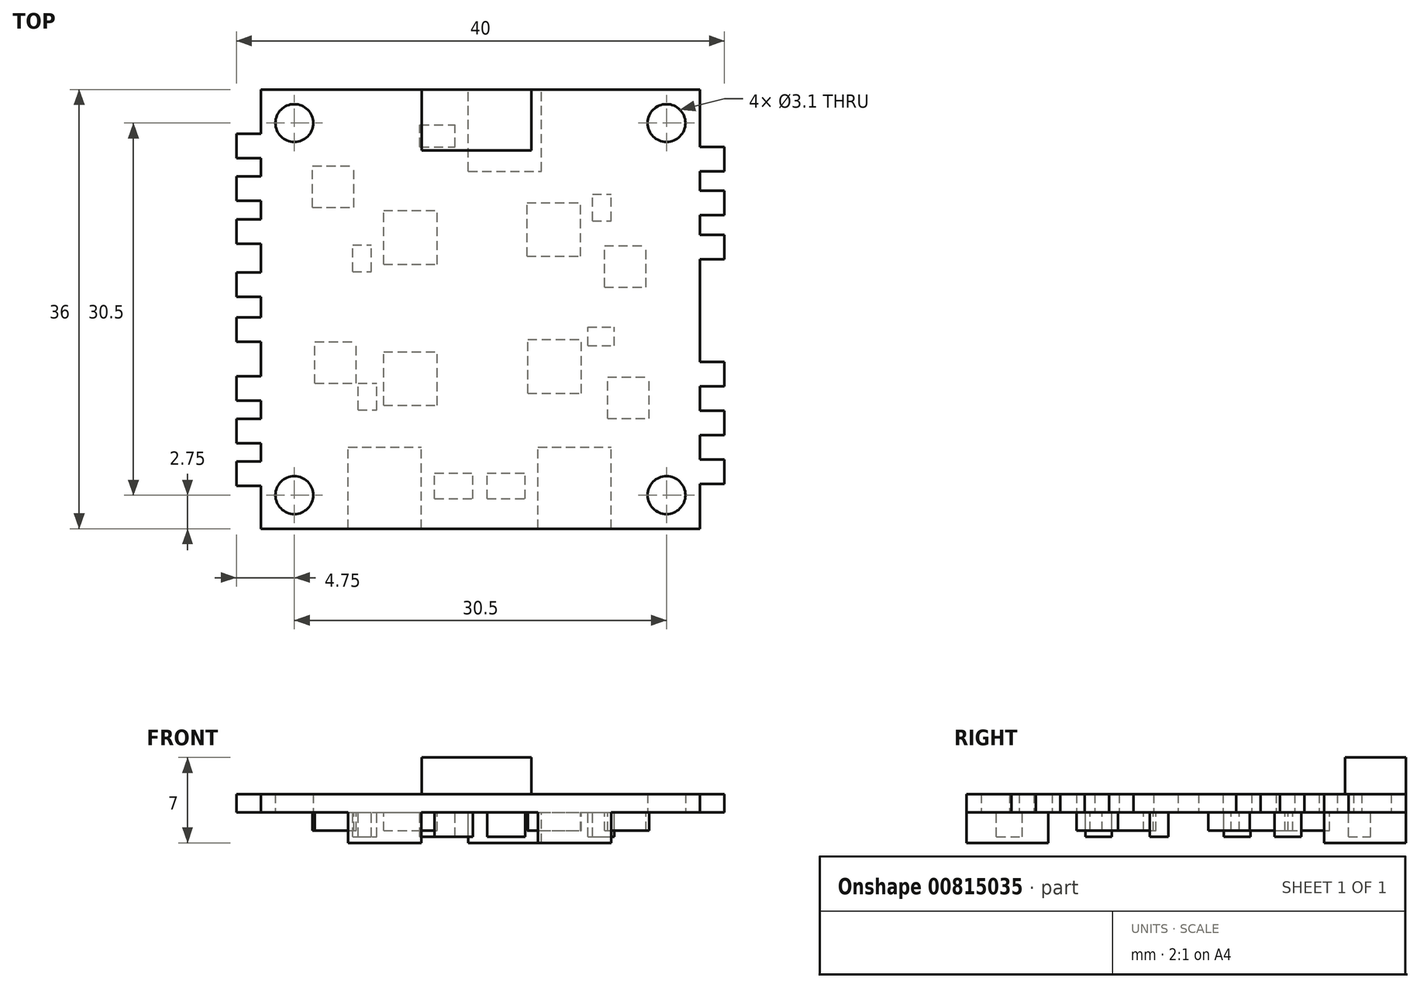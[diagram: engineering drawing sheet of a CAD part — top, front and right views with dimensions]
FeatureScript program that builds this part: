
annotation { "Feature Type Name" : "Feature", "Feature Type Description" : "" }
export const myFeature = defineFeature(function(context is Context, id is Id, definition is map)
    precondition{}
    {
        {
            var Q0;
            Q0=qCreatedBy(makeId("Top.planeOp"),FACE);
            var sketch = newSketch(context, id + "F0", { "sketchPlane" : qUnion([Q0])});
            skLineSegment(sketch, "E0", {"start": v(-20.18, -18) * mm, "end": v(20.18, 18) * mm, "construction": true});
            skPoint(sketch, "E1", {"position": v(-15.42, 15.08) * mm});
            skPoint(sketch, "E2", {"position": v(-15.47, -15.18) * mm});
            skPoint(sketch, "E3", {"position": v(14.98, 15.03) * mm});
            skPoint(sketch, "E4", {"position": v(15.18, -15.28) * mm});
            skSolve(sketch);
        }
        {
            var Q0;
            Q0=qCreatedBy(makeId("Top.planeOp"),FACE);
            var sketch = newSketch(context, id + "F1", { "sketchPlane" : qUnion([Q0])});
            skLineSegment(sketch, "E5", {"start": v(-20.13, -18) * mm, "end": v(20.13, 18) * mm, "construction": true});
            skSolve(sketch);
        }
        {
            var Q0;
            Q0=qCreatedBy(makeId("Top.planeOp"),FACE);
            var sketch = newSketch(context, id + "F2", { "sketchPlane" : qUnion([Q0])});
            skLineSegment(sketch, "E6.bottom", {"start": v(-18, 18) * mm, "end": v(18, 18) * mm});
            skLineSegment(sketch, "E6.top", {"start": v(-18, -18) * mm, "end": v(18, -18) * mm});
            skLineSegment(sketch, "E6.left", {"start": v(-18, 18) * mm, "end": v(-18, -18) * mm});
            skLineSegment(sketch, "E6.right", {"start": v(18, 18) * mm, "end": v(18, -18) * mm});
            skLineSegment(sketch, "E7", {"start": v(-18, 18) * mm, "end": v(18, -18) * mm, "construction": true});
            skLineSegment(sketch, "E8.bottom", {"start": v(-20, 14.37) * mm, "end": v(-18, 14.37) * mm});
            skLineSegment(sketch, "E8.top", {"start": v(-20, 12.37) * mm, "end": v(-18, 12.37) * mm});
            skLineSegment(sketch, "E8.left", {"start": v(-20, 14.37) * mm, "end": v(-20, 12.37) * mm});
            skLineSegment(sketch, "E8.right", {"start": v(-18, 14.37) * mm, "end": v(-18, 12.37) * mm});
            skLineSegment(sketch, "E9.1.0.0", {"start": v(-20, 10.87) * mm, "end": v(-18, 10.87) * mm});
            skLineSegment(sketch, "E9.1.0.1", {"start": v(-20, 8.87) * mm, "end": v(-18, 8.87) * mm});
            skLineSegment(sketch, "E9.1.0.2", {"start": v(-20, 10.87) * mm, "end": v(-20, 8.87) * mm});
            skLineSegment(sketch, "E9.1.0.3", {"start": v(-18, 10.87) * mm, "end": v(-18, 8.87) * mm});
            skLineSegment(sketch, "E9.2.0.0", {"start": v(-20, 7.37) * mm, "end": v(-18, 7.37) * mm});
            skLineSegment(sketch, "E9.2.0.1", {"start": v(-20, 5.37) * mm, "end": v(-18, 5.37) * mm});
            skLineSegment(sketch, "E9.2.0.2", {"start": v(-20, 7.37) * mm, "end": v(-20, 5.37) * mm});
            skLineSegment(sketch, "E9.2.0.3", {"start": v(-18, 7.37) * mm, "end": v(-18, 5.37) * mm});
            skLineSegment(sketch, "E9.direction1", {"start": v(-20, 12.37) * mm, "end": v(-20, 8.87) * mm, "construction": true});
            skLineSegment(sketch, "E10.bottom", {"start": v(-20, -5.5) * mm, "end": v(-18, -5.5) * mm});
            skLineSegment(sketch, "E10.top", {"start": v(-20, -7.5) * mm, "end": v(-18, -7.5) * mm});
            skLineSegment(sketch, "E10.left", {"start": v(-20, -5.5) * mm, "end": v(-20, -7.5) * mm});
            skLineSegment(sketch, "E10.right", {"start": v(-18, -5.5) * mm, "end": v(-18, -7.5) * mm});
            skLineSegment(sketch, "E11.1.0.0", {"start": v(-20, -9) * mm, "end": v(-18, -9) * mm});
            skLineSegment(sketch, "E11.1.0.1", {"start": v(-20, -11) * mm, "end": v(-18, -11) * mm});
            skLineSegment(sketch, "E11.1.0.2", {"start": v(-20, -9) * mm, "end": v(-20, -11) * mm});
            skLineSegment(sketch, "E11.1.0.3", {"start": v(-18, -9) * mm, "end": v(-18, -11) * mm});
            skLineSegment(sketch, "E11.2.0.0", {"start": v(-20, -12.5) * mm, "end": v(-18, -12.5) * mm});
            skLineSegment(sketch, "E11.2.0.1", {"start": v(-20, -14.5) * mm, "end": v(-18, -14.5) * mm});
            skLineSegment(sketch, "E11.2.0.2", {"start": v(-20, -12.5) * mm, "end": v(-20, -14.5) * mm});
            skLineSegment(sketch, "E11.2.0.3", {"start": v(-18, -12.5) * mm, "end": v(-18, -14.5) * mm});
            skLineSegment(sketch, "E11.direction1", {"start": v(-20, -7.5) * mm, "end": v(-20, -11) * mm, "construction": true});
            skLineSegment(sketch, "E12.bottom", {"start": v(18, 13.3) * mm, "end": v(20, 13.3) * mm});
            skLineSegment(sketch, "E12.top", {"start": v(18, 11.3) * mm, "end": v(20, 11.3) * mm});
            skLineSegment(sketch, "E12.left", {"start": v(18, 13.3) * mm, "end": v(18, 11.3) * mm});
            skLineSegment(sketch, "E12.right", {"start": v(20, 13.3) * mm, "end": v(20, 11.3) * mm});
            skLineSegment(sketch, "E13.1.0.0", {"start": v(18, 9.7) * mm, "end": v(20, 9.7) * mm});
            skLineSegment(sketch, "E13.1.0.1", {"start": v(18, 7.7) * mm, "end": v(20, 7.7) * mm});
            skLineSegment(sketch, "E13.1.0.2", {"start": v(18, 9.7) * mm, "end": v(18, 7.7) * mm});
            skLineSegment(sketch, "E13.1.0.3", {"start": v(20, 9.7) * mm, "end": v(20, 7.7) * mm});
            skLineSegment(sketch, "E13.2.0.0", {"start": v(18, 6.1) * mm, "end": v(20, 6.1) * mm});
            skLineSegment(sketch, "E13.2.0.1", {"start": v(18, 4.1) * mm, "end": v(20, 4.1) * mm});
            skLineSegment(sketch, "E13.2.0.2", {"start": v(18, 6.1) * mm, "end": v(18, 4.1) * mm});
            skLineSegment(sketch, "E13.2.0.3", {"start": v(20, 6.1) * mm, "end": v(20, 4.1) * mm});
            skLineSegment(sketch, "E13.direction1", {"start": v(18, 11.3) * mm, "end": v(18, 7.7) * mm, "construction": true});
            skLineSegment(sketch, "E14.bottom", {"start": v(18, -4.32) * mm, "end": v(20, -4.32) * mm});
            skLineSegment(sketch, "E14.top", {"start": v(18, -6.32) * mm, "end": v(20, -6.32) * mm});
            skLineSegment(sketch, "E14.left", {"start": v(18, -4.32) * mm, "end": v(18, -6.32) * mm});
            skLineSegment(sketch, "E14.right", {"start": v(20, -4.32) * mm, "end": v(20, -6.32) * mm});
            skLineSegment(sketch, "E15.1.0.0", {"start": v(18, -8.32) * mm, "end": v(20, -8.32) * mm});
            skLineSegment(sketch, "E15.1.0.1", {"start": v(18, -10.32) * mm, "end": v(20, -10.32) * mm});
            skLineSegment(sketch, "E15.1.0.2", {"start": v(18, -8.32) * mm, "end": v(18, -10.32) * mm});
            skLineSegment(sketch, "E15.1.0.3", {"start": v(20, -8.32) * mm, "end": v(20, -10.32) * mm});
            skLineSegment(sketch, "E15.2.0.0", {"start": v(18, -12.32) * mm, "end": v(20, -12.32) * mm});
            skLineSegment(sketch, "E15.2.0.1", {"start": v(18, -14.32) * mm, "end": v(20, -14.32) * mm});
            skLineSegment(sketch, "E15.2.0.2", {"start": v(18, -12.32) * mm, "end": v(18, -14.32) * mm});
            skLineSegment(sketch, "E15.2.0.3", {"start": v(20, -12.32) * mm, "end": v(20, -14.32) * mm});
            skLineSegment(sketch, "E15.direction1", {"start": v(18, -6.32) * mm, "end": v(18, -10.32) * mm, "construction": true});
            skLineSegment(sketch, "E16.bottom", {"start": v(15.25, -15.25) * mm, "end": v(-15.25, -15.25) * mm, "construction": true});
            skLineSegment(sketch, "E16.top", {"start": v(15.25, 15.25) * mm, "end": v(-15.25, 15.25) * mm, "construction": true});
            skLineSegment(sketch, "E16.left", {"start": v(15.25, -15.25) * mm, "end": v(15.25, 15.25) * mm, "construction": true});
            skLineSegment(sketch, "E16.right", {"start": v(-15.25, -15.25) * mm, "end": v(-15.25, 15.25) * mm, "construction": true});
            skPoint(sketch, "E16.middle", {"position": v(0, 0) * mm});
            skCircle(sketch, "E17", {"center": v(-15.25, 15.25) * mm, "radius": 1.55 * mm});
            skCircle(sketch, "E18", {"center": v(15.25, 15.25) * mm, "radius": 1.55 * mm});
            skCircle(sketch, "E19", {"center": v(15.25, -15.25) * mm, "radius": 1.55 * mm});
            skCircle(sketch, "E20", {"center": v(-15.25, -15.25) * mm, "radius": 1.55 * mm});
            skLineSegment(sketch, "E21.2.0.0", {"start": v(-20, -0.67) * mm, "end": v(-18, -0.67) * mm});
            skLineSegment(sketch, "E21.2.0.1", {"start": v(-20, -2.67) * mm, "end": v(-18, -2.67) * mm});
            skLineSegment(sketch, "E21.2.0.2", {"start": v(-20, -0.67) * mm, "end": v(-20, -2.67) * mm});
            skLineSegment(sketch, "E21.2.0.3", {"start": v(-18, -0.67) * mm, "end": v(-18, -2.67) * mm});
            skLineSegment(sketch, "E22.2.0.0", {"start": v(-20, 3) * mm, "end": v(-18, 3) * mm});
            skLineSegment(sketch, "E22.2.0.1", {"start": v(-20, 1) * mm, "end": v(-18, 1) * mm});
            skLineSegment(sketch, "E22.2.0.2", {"start": v(-20, 3) * mm, "end": v(-20, 1) * mm});
            skLineSegment(sketch, "E22.2.0.3", {"start": v(-18, 3) * mm, "end": v(-18, 1) * mm});
            skSolve(sketch);
        }
        {
            var Q0;
            Q0 = qSketchRegion(id + "F2", true);
            extrude(context, id + "F3", {"entities" : qUnion([Q0]), "depth" : 1.5 * mm, "offsetDistance" : 25 * mm});
        }
        {
            var Q0;
            Q0=makeQuery(id+"F3.opExtrude","CAP_FACE",FACE,{"disambiguationData":[OSD([sQuery(id+"F2.wireOp",EDGE,"E6.bottom"),sQuery(id+"F2.wireOp",EDGE,"E6.top"),sQuery(id+"F2.wireOp",EDGE,"E6.left"),sQuery(id+"F2.wireOp",EDGE,"E6.right"),sQuery(id+"F2.wireOp",EDGE,"E8.bottom"),sQuery(id+"F2.wireOp",EDGE,"E8.top"),sQuery(id+"F2.wireOp",EDGE,"E8.left"),sQuery(id+"F2.wireOp",EDGE,"E9.1.0.0"),sQuery(id+"F2.wireOp",EDGE,"E9.1.0.1"),sQuery(id+"F2.wireOp",EDGE,"E9.1.0.2"),sQuery(id+"F2.wireOp",EDGE,"E9.2.0.0"),sQuery(id+"F2.wireOp",EDGE,"E9.2.0.1"),sQuery(id+"F2.wireOp",EDGE,"E9.2.0.2"),sQuery(id+"F2.wireOp",EDGE,"E10.bottom"),sQuery(id+"F2.wireOp",EDGE,"E10.top"),sQuery(id+"F2.wireOp",EDGE,"E10.left"),sQuery(id+"F2.wireOp",EDGE,"E11.1.0.0"),sQuery(id+"F2.wireOp",EDGE,"E11.1.0.1"),sQuery(id+"F2.wireOp",EDGE,"E11.1.0.2"),sQuery(id+"F2.wireOp",EDGE,"E11.2.0.0"),sQuery(id+"F2.wireOp",EDGE,"E11.2.0.1"),sQuery(id+"F2.wireOp",EDGE,"E11.2.0.2"),sQuery(id+"F2.wireOp",EDGE,"E12.bottom"),sQuery(id+"F2.wireOp",EDGE,"E12.top"),sQuery(id+"F2.wireOp",EDGE,"E12.right"),sQuery(id+"F2.wireOp",EDGE,"E13.1.0.0"),sQuery(id+"F2.wireOp",EDGE,"E13.1.0.1"),sQuery(id+"F2.wireOp",EDGE,"E13.1.0.3"),sQuery(id+"F2.wireOp",EDGE,"E13.2.0.0"),sQuery(id+"F2.wireOp",EDGE,"E13.2.0.1"),sQuery(id+"F2.wireOp",EDGE,"E13.2.0.3"),sQuery(id+"F2.wireOp",EDGE,"E14.bottom"),sQuery(id+"F2.wireOp",EDGE,"E14.top"),sQuery(id+"F2.wireOp",EDGE,"E14.right"),sQuery(id+"F2.wireOp",EDGE,"E15.1.0.0"),sQuery(id+"F2.wireOp",EDGE,"E15.1.0.1"),sQuery(id+"F2.wireOp",EDGE,"E15.1.0.3"),sQuery(id+"F2.wireOp",EDGE,"E15.2.0.0"),sQuery(id+"F2.wireOp",EDGE,"E15.2.0.1"),sQuery(id+"F2.wireOp",EDGE,"E15.2.0.3"),sQuery(id+"F2.wireOp",EDGE,"E17"),sQuery(id+"F2.wireOp",EDGE,"E18"),sQuery(id+"F2.wireOp",EDGE,"E19"),sQuery(id+"F2.wireOp",EDGE,"E20")])],"isStart":false});
            var sketch = newSketch(context, id + "F4", { "sketchPlane" : qUnion([Q0])});
            skLineSegment(sketch, "E23.bottom", {"start": v(-4.82, 18) * mm, "end": v(4.18, 18) * mm});
            skLineSegment(sketch, "E23.top", {"start": v(-4.82, 13) * mm, "end": v(4.18, 13) * mm});
            skLineSegment(sketch, "E23.left", {"start": v(-4.82, 18) * mm, "end": v(-4.82, 13) * mm});
            skLineSegment(sketch, "E23.right", {"start": v(4.18, 18) * mm, "end": v(4.18, 13) * mm});
            skSolve(sketch);
        }
        {
            var Q0;
            Q0 = qSketchRegion(id + "F4", true);
            extrude(context, id + "F5", {"entities" : qUnion([Q0]), "operationType" : NewBodyOperationType.ADD, "depth" : 3 * mm, "offsetDistance" : 25 * mm});
        }
        {
            var Q0;
            Q0=makeQuery(id+"F3.opExtrude","CAP_FACE",FACE,{"disambiguationData":[OSD([sQuery(id+"F2.wireOp",EDGE,"E6.bottom"),sQuery(id+"F2.wireOp",EDGE,"E6.top"),sQuery(id+"F2.wireOp",EDGE,"E6.left"),sQuery(id+"F2.wireOp",EDGE,"E6.right"),sQuery(id+"F2.wireOp",EDGE,"E8.bottom"),sQuery(id+"F2.wireOp",EDGE,"E8.top"),sQuery(id+"F2.wireOp",EDGE,"E8.left"),sQuery(id+"F2.wireOp",EDGE,"E9.1.0.0"),sQuery(id+"F2.wireOp",EDGE,"E9.1.0.1"),sQuery(id+"F2.wireOp",EDGE,"E9.1.0.2"),sQuery(id+"F2.wireOp",EDGE,"E9.2.0.0"),sQuery(id+"F2.wireOp",EDGE,"E9.2.0.1"),sQuery(id+"F2.wireOp",EDGE,"E9.2.0.2"),sQuery(id+"F2.wireOp",EDGE,"E10.bottom"),sQuery(id+"F2.wireOp",EDGE,"E10.top"),sQuery(id+"F2.wireOp",EDGE,"E10.left"),sQuery(id+"F2.wireOp",EDGE,"E11.1.0.0"),sQuery(id+"F2.wireOp",EDGE,"E11.1.0.1"),sQuery(id+"F2.wireOp",EDGE,"E11.1.0.2"),sQuery(id+"F2.wireOp",EDGE,"E11.2.0.0"),sQuery(id+"F2.wireOp",EDGE,"E11.2.0.1"),sQuery(id+"F2.wireOp",EDGE,"E11.2.0.2"),sQuery(id+"F2.wireOp",EDGE,"E12.bottom"),sQuery(id+"F2.wireOp",EDGE,"E12.top"),sQuery(id+"F2.wireOp",EDGE,"E12.right"),sQuery(id+"F2.wireOp",EDGE,"E13.1.0.0"),sQuery(id+"F2.wireOp",EDGE,"E13.1.0.1"),sQuery(id+"F2.wireOp",EDGE,"E13.1.0.3"),sQuery(id+"F2.wireOp",EDGE,"E13.2.0.0"),sQuery(id+"F2.wireOp",EDGE,"E13.2.0.1"),sQuery(id+"F2.wireOp",EDGE,"E13.2.0.3"),sQuery(id+"F2.wireOp",EDGE,"E14.bottom"),sQuery(id+"F2.wireOp",EDGE,"E14.top"),sQuery(id+"F2.wireOp",EDGE,"E14.right"),sQuery(id+"F2.wireOp",EDGE,"E15.1.0.0"),sQuery(id+"F2.wireOp",EDGE,"E15.1.0.1"),sQuery(id+"F2.wireOp",EDGE,"E15.1.0.3"),sQuery(id+"F2.wireOp",EDGE,"E15.2.0.0"),sQuery(id+"F2.wireOp",EDGE,"E15.2.0.1"),sQuery(id+"F2.wireOp",EDGE,"E15.2.0.3"),sQuery(id+"F2.wireOp",EDGE,"E17"),sQuery(id+"F2.wireOp",EDGE,"E18"),sQuery(id+"F2.wireOp",EDGE,"E19"),sQuery(id+"F2.wireOp",EDGE,"E20")])],"isStart":true});
            var sketch = newSketch(context, id + "F6", { "sketchPlane" : qUnion([Q0])});
            skLineSegment(sketch, "E24.bottom", {"start": v(-7.93, 7.89) * mm, "end": v(-3.53, 7.89) * mm});
            skLineSegment(sketch, "E24.top", {"start": v(-7.93, 3.49) * mm, "end": v(-3.53, 3.49) * mm});
            skLineSegment(sketch, "E24.left", {"start": v(-7.93, 7.89) * mm, "end": v(-7.93, 3.49) * mm});
            skLineSegment(sketch, "E24.right", {"start": v(-3.53, 7.89) * mm, "end": v(-3.53, 3.49) * mm});
            skLineSegment(sketch, "E25.bottom", {"start": v(-7.93, -3.69) * mm, "end": v(-3.53, -3.69) * mm});
            skLineSegment(sketch, "E25.top", {"start": v(-7.93, -8.09) * mm, "end": v(-3.53, -8.09) * mm});
            skLineSegment(sketch, "E25.left", {"start": v(-7.93, -3.69) * mm, "end": v(-7.93, -8.09) * mm});
            skLineSegment(sketch, "E25.right", {"start": v(-3.53, -3.69) * mm, "end": v(-3.53, -8.09) * mm});
            skLineSegment(sketch, "E26.bottom", {"start": v(3.88, 6.9) * mm, "end": v(8.28, 6.9) * mm});
            skLineSegment(sketch, "E26.top", {"start": v(3.88, 2.5) * mm, "end": v(8.28, 2.5) * mm});
            skLineSegment(sketch, "E26.left", {"start": v(3.88, 6.9) * mm, "end": v(3.88, 2.5) * mm});
            skLineSegment(sketch, "E26.right", {"start": v(8.28, 6.9) * mm, "end": v(8.28, 2.5) * mm});
            skLineSegment(sketch, "E27.bottom", {"start": v(3.81, -4.33) * mm, "end": v(8.21, -4.33) * mm});
            skLineSegment(sketch, "E27.top", {"start": v(3.81, -8.73) * mm, "end": v(8.21, -8.73) * mm});
            skLineSegment(sketch, "E27.left", {"start": v(3.81, -4.33) * mm, "end": v(3.81, -8.73) * mm});
            skLineSegment(sketch, "E27.right", {"start": v(8.21, -4.33) * mm, "end": v(8.21, -8.73) * mm});
            skLineSegment(sketch, "E28.bottom", {"start": v(10.16, -1.8) * mm, "end": v(13.56, -1.8) * mm});
            skLineSegment(sketch, "E28.top", {"start": v(10.16, -5.2) * mm, "end": v(13.56, -5.2) * mm});
            skLineSegment(sketch, "E28.left", {"start": v(10.16, -1.8) * mm, "end": v(10.16, -5.2) * mm});
            skLineSegment(sketch, "E28.right", {"start": v(13.56, -1.8) * mm, "end": v(13.56, -5.2) * mm});
            skLineSegment(sketch, "E29.bottom", {"start": v(-13.76, -8.34) * mm, "end": v(-10.36, -8.34) * mm});
            skLineSegment(sketch, "E29.top", {"start": v(-13.76, -11.74) * mm, "end": v(-10.36, -11.74) * mm});
            skLineSegment(sketch, "E29.left", {"start": v(-13.76, -8.34) * mm, "end": v(-13.76, -11.74) * mm});
            skLineSegment(sketch, "E29.right", {"start": v(-10.36, -8.34) * mm, "end": v(-10.36, -11.74) * mm});
            skLineSegment(sketch, "E30.bottom", {"start": v(-13.57, 6.09) * mm, "end": v(-10.17, 6.09) * mm});
            skLineSegment(sketch, "E30.top", {"start": v(-13.57, 2.69) * mm, "end": v(-10.17, 2.69) * mm});
            skLineSegment(sketch, "E30.left", {"start": v(-13.57, 6.09) * mm, "end": v(-13.57, 2.69) * mm});
            skLineSegment(sketch, "E30.right", {"start": v(-10.17, 6.09) * mm, "end": v(-10.17, 2.69) * mm});
            skLineSegment(sketch, "E31.bottom", {"start": v(10.42, 8.98) * mm, "end": v(13.82, 8.98) * mm});
            skLineSegment(sketch, "E31.top", {"start": v(10.42, 5.58) * mm, "end": v(13.82, 5.58) * mm});
            skLineSegment(sketch, "E31.left", {"start": v(10.42, 8.98) * mm, "end": v(10.42, 5.58) * mm});
            skLineSegment(sketch, "E31.right", {"start": v(13.82, 8.98) * mm, "end": v(13.82, 5.58) * mm});
            skLineSegment(sketch, "E32.bottom", {"start": v(-1, -11.3) * mm, "end": v(5, -11.3) * mm});
            skLineSegment(sketch, "E32.top", {"start": v(-1, -18) * mm, "end": v(5, -18) * mm});
            skLineSegment(sketch, "E32.left", {"start": v(-1, -11.3) * mm, "end": v(-1, -18) * mm});
            skLineSegment(sketch, "E32.right", {"start": v(5, -11.3) * mm, "end": v(5, -18) * mm});
            skLineSegment(sketch, "E33.bottom", {"start": v(-3.75, 15.55) * mm, "end": v(-0.61, 15.55) * mm});
            skLineSegment(sketch, "E33.top", {"start": v(-3.75, 13.44) * mm, "end": v(-0.61, 13.44) * mm});
            skLineSegment(sketch, "E33.left", {"start": v(-3.75, 15.55) * mm, "end": v(-3.75, 13.44) * mm});
            skLineSegment(sketch, "E33.right", {"start": v(-0.61, 15.55) * mm, "end": v(-0.61, 13.44) * mm});
            skLineSegment(sketch, "E34.bottom", {"start": v(0.54, 15.55) * mm, "end": v(3.68, 15.55) * mm});
            skLineSegment(sketch, "E34.top", {"start": v(0.54, 13.44) * mm, "end": v(3.68, 13.44) * mm});
            skLineSegment(sketch, "E34.left", {"start": v(0.54, 15.55) * mm, "end": v(0.54, 13.44) * mm});
            skLineSegment(sketch, "E34.right", {"start": v(3.68, 15.55) * mm, "end": v(3.68, 13.44) * mm});
            skLineSegment(sketch, "E35.bottom", {"start": v(-4.95, -13.3) * mm, "end": v(-2.08, -13.3) * mm});
            skLineSegment(sketch, "E35.top", {"start": v(-4.95, -15.1) * mm, "end": v(-2.08, -15.1) * mm});
            skLineSegment(sketch, "E35.left", {"start": v(-4.95, -13.3) * mm, "end": v(-4.95, -15.1) * mm});
            skLineSegment(sketch, "E35.right", {"start": v(-2.08, -13.3) * mm, "end": v(-2.08, -15.1) * mm});
            skLineSegment(sketch, "E36.bottom", {"start": v(-10.47, -3.08) * mm, "end": v(-8.93, -3.08) * mm});
            skLineSegment(sketch, "E36.top", {"start": v(-10.47, -5.26) * mm, "end": v(-8.93, -5.26) * mm});
            skLineSegment(sketch, "E36.left", {"start": v(-10.47, -3.08) * mm, "end": v(-10.47, -5.26) * mm});
            skLineSegment(sketch, "E36.right", {"start": v(-8.93, -3.08) * mm, "end": v(-8.93, -5.26) * mm});
            skLineSegment(sketch, "E37.bottom", {"start": v(9.18, -7.24) * mm, "end": v(10.72, -7.24) * mm});
            skLineSegment(sketch, "E37.top", {"start": v(9.18, -9.42) * mm, "end": v(10.72, -9.42) * mm});
            skLineSegment(sketch, "E37.left", {"start": v(9.18, -7.24) * mm, "end": v(9.18, -9.42) * mm});
            skLineSegment(sketch, "E37.right", {"start": v(10.72, -7.24) * mm, "end": v(10.72, -9.42) * mm});
            skLineSegment(sketch, "E38.bottom", {"start": v(8.8, 3) * mm, "end": v(10.98, 3) * mm});
            skLineSegment(sketch, "E38.top", {"start": v(8.8, 1.47) * mm, "end": v(10.98, 1.47) * mm});
            skLineSegment(sketch, "E38.left", {"start": v(8.8, 3) * mm, "end": v(8.8, 1.47) * mm});
            skLineSegment(sketch, "E38.right", {"start": v(10.98, 3) * mm, "end": v(10.98, 1.47) * mm});
            skLineSegment(sketch, "E39.bottom", {"start": v(-10.85, 18) * mm, "end": v(-4.85, 18) * mm});
            skLineSegment(sketch, "E39.top", {"start": v(-10.85, 11.3) * mm, "end": v(-4.85, 11.3) * mm});
            skLineSegment(sketch, "E39.left", {"start": v(-10.85, 18) * mm, "end": v(-10.85, 11.3) * mm});
            skLineSegment(sketch, "E39.right", {"start": v(-4.85, 18) * mm, "end": v(-4.85, 11.3) * mm});
            skLineSegment(sketch, "E40.bottom", {"start": v(4.71, 18) * mm, "end": v(10.71, 18) * mm});
            skLineSegment(sketch, "E40.top", {"start": v(4.71, 11.3) * mm, "end": v(10.71, 11.3) * mm});
            skLineSegment(sketch, "E40.left", {"start": v(4.71, 18) * mm, "end": v(4.71, 11.3) * mm});
            skLineSegment(sketch, "E40.right", {"start": v(10.71, 18) * mm, "end": v(10.71, 11.3) * mm});
            skPoint(sketch, "E41.oppositeSnap0", {"position": v(-11.87, 6.09) * mm});
            skLineSegment(sketch, "E41.bottom", {"start": v(-10.02, 8.27) * mm, "end": v(-8.49, 8.27) * mm});
            skLineSegment(sketch, "E41.top", {"start": v(-10.02, 6.09) * mm, "end": v(-8.49, 6.09) * mm});
            skLineSegment(sketch, "E41.left", {"start": v(-10.02, 8.27) * mm, "end": v(-10.02, 6.09) * mm});
            skLineSegment(sketch, "E41.right", {"start": v(-8.49, 8.27) * mm, "end": v(-8.49, 6.09) * mm});
            skSolve(sketch);
        }
        {
            var Q0;
            Q0=makeQuery(id+"F6.imprint","IMPRINT",FACE,{"disambiguationData":[TD([[makeQuery(id+"F6.imprint","IMPRINT",EDGE,{"derivedFrom":sQuery(id+"F6.wireOp",EDGE,"E32.bottom")}),-1.0]])]});
            var Q1;
            Q1=makeQuery(id+"F6.imprint","IMPRINT",FACE,{"disambiguationData":[TD([[makeQuery(id+"F6.imprint","IMPRINT",EDGE,{"derivedFrom":sQuery(id+"F6.wireOp",EDGE,"E39.bottom")}),-1.0]])]});
            var Q2;
            Q2=makeQuery(id+"F6.imprint","IMPRINT",FACE,{"disambiguationData":[TD([[makeQuery(id+"F6.imprint","IMPRINT",EDGE,{"derivedFrom":sQuery(id+"F6.wireOp",EDGE,"E40.bottom")}),-1.0]])]});
            extrude(context, id + "F7", {"entities" : qUnion([Q0, Q1, Q2]), "operationType" : NewBodyOperationType.ADD, "depth" : 2.5 * mm, "offsetDistance" : 25 * mm});
        }
        {
            var Q0;
            Q0=makeQuery(id+"F6.imprint","IMPRINT",FACE,{"disambiguationData":[TD([[makeQuery(id+"F6.imprint","IMPRINT",EDGE,{"derivedFrom":sQuery(id+"F6.wireOp",EDGE,"E29.bottom")}),-1.0]])]});
            var Q1;
            Q1=makeQuery(id+"F6.imprint","IMPRINT",FACE,{"disambiguationData":[TD([[makeQuery(id+"F6.imprint","IMPRINT",EDGE,{"derivedFrom":sQuery(id+"F6.wireOp",EDGE,"E25.bottom")}),-1.0]])]});
            var Q2;
            Q2=makeQuery(id+"F6.imprint","IMPRINT",FACE,{"disambiguationData":[TD([[makeQuery(id+"F6.imprint","IMPRINT",EDGE,{"derivedFrom":sQuery(id+"F6.wireOp",EDGE,"E27.bottom")}),-1.0]])]});
            var Q3;
            Q3=makeQuery(id+"F6.imprint","IMPRINT",FACE,{"disambiguationData":[TD([[makeQuery(id+"F6.imprint","IMPRINT",EDGE,{"derivedFrom":sQuery(id+"F6.wireOp",EDGE,"E28.bottom")}),-1.0]])]});
            var Q4;
            Q4=makeQuery(id+"F6.imprint","IMPRINT",FACE,{"disambiguationData":[TD([[makeQuery(id+"F6.imprint","IMPRINT",EDGE,{"derivedFrom":sQuery(id+"F6.wireOp",EDGE,"E31.bottom")}),-1.0]])]});
            var Q5;
            Q5=makeQuery(id+"F6.imprint","IMPRINT",FACE,{"disambiguationData":[TD([[makeQuery(id+"F6.imprint","IMPRINT",EDGE,{"derivedFrom":sQuery(id+"F6.wireOp",EDGE,"E26.bottom")}),-1.0]])]});
            var Q6;
            Q6=makeQuery(id+"F6.imprint","IMPRINT",FACE,{"disambiguationData":[TD([[makeQuery(id+"F6.imprint","IMPRINT",EDGE,{"derivedFrom":sQuery(id+"F6.wireOp",EDGE,"E24.bottom")}),-1.0]])]});
            var Q7;
            Q7=makeQuery(id+"F6.imprint","IMPRINT",FACE,{"disambiguationData":[TD([[makeQuery(id+"F6.imprint","IMPRINT",EDGE,{"derivedFrom":sQuery(id+"F6.wireOp",EDGE,"E30.bottom")}),-1.0]])]});
            extrude(context, id + "F8", {"entities" : qUnion([Q0, Q1, Q2, Q3, Q4, Q5, Q6, Q7]), "operationType" : NewBodyOperationType.ADD, "depth" : 1.5 * mm, "offsetDistance" : 25 * mm});
        }
        {
            var Q0;
            Q0=makeQuery(id+"F6.imprint","IMPRINT",FACE,{"disambiguationData":[TD([[makeQuery(id+"F6.imprint","IMPRINT",EDGE,{"derivedFrom":sQuery(id+"F6.wireOp",EDGE,"E36.bottom")}),-1.0]])]});
            var Q1;
            Q1=makeQuery(id+"F6.imprint","IMPRINT",FACE,{"disambiguationData":[TD([[makeQuery(id+"F6.imprint","IMPRINT",EDGE,{"derivedFrom":sQuery(id+"F6.wireOp",EDGE,"E41.bottom")}),-1.0]])]});
            var Q2;
            Q2=makeQuery(id+"F6.imprint","IMPRINT",FACE,{"disambiguationData":[TD([[makeQuery(id+"F6.imprint","IMPRINT",EDGE,{"derivedFrom":sQuery(id+"F6.wireOp",EDGE,"E37.bottom")}),-1.0]])]});
            var Q3;
            Q3=makeQuery(id+"F6.imprint","IMPRINT",FACE,{"disambiguationData":[TD([[makeQuery(id+"F6.imprint","IMPRINT",EDGE,{"derivedFrom":sQuery(id+"F6.wireOp",EDGE,"E35.bottom")}),-1.0]])]});
            var Q4;
            Q4=makeQuery(id+"F6.imprint","IMPRINT",FACE,{"disambiguationData":[TD([[makeQuery(id+"F6.imprint","IMPRINT",EDGE,{"derivedFrom":sQuery(id+"F6.wireOp",EDGE,"E38.bottom")}),-1.0]])]});
            var Q5;
            Q5=makeQuery(id+"F6.imprint","IMPRINT",FACE,{"disambiguationData":[TD([[makeQuery(id+"F6.imprint","IMPRINT",EDGE,{"derivedFrom":sQuery(id+"F6.wireOp",EDGE,"E33.bottom")}),-1.0]])]});
            var Q6;
            Q6=makeQuery(id+"F6.imprint","IMPRINT",FACE,{"disambiguationData":[TD([[makeQuery(id+"F6.imprint","IMPRINT",EDGE,{"derivedFrom":sQuery(id+"F6.wireOp",EDGE,"E34.bottom")}),-1.0]])]});
            extrude(context, id + "F9", {"entities" : qUnion([Q0, Q1, Q2, Q3, Q4, Q5, Q6]), "operationType" : NewBodyOperationType.ADD, "depth" : 2 * mm, "offsetDistance" : 25 * mm});
        }
    });
